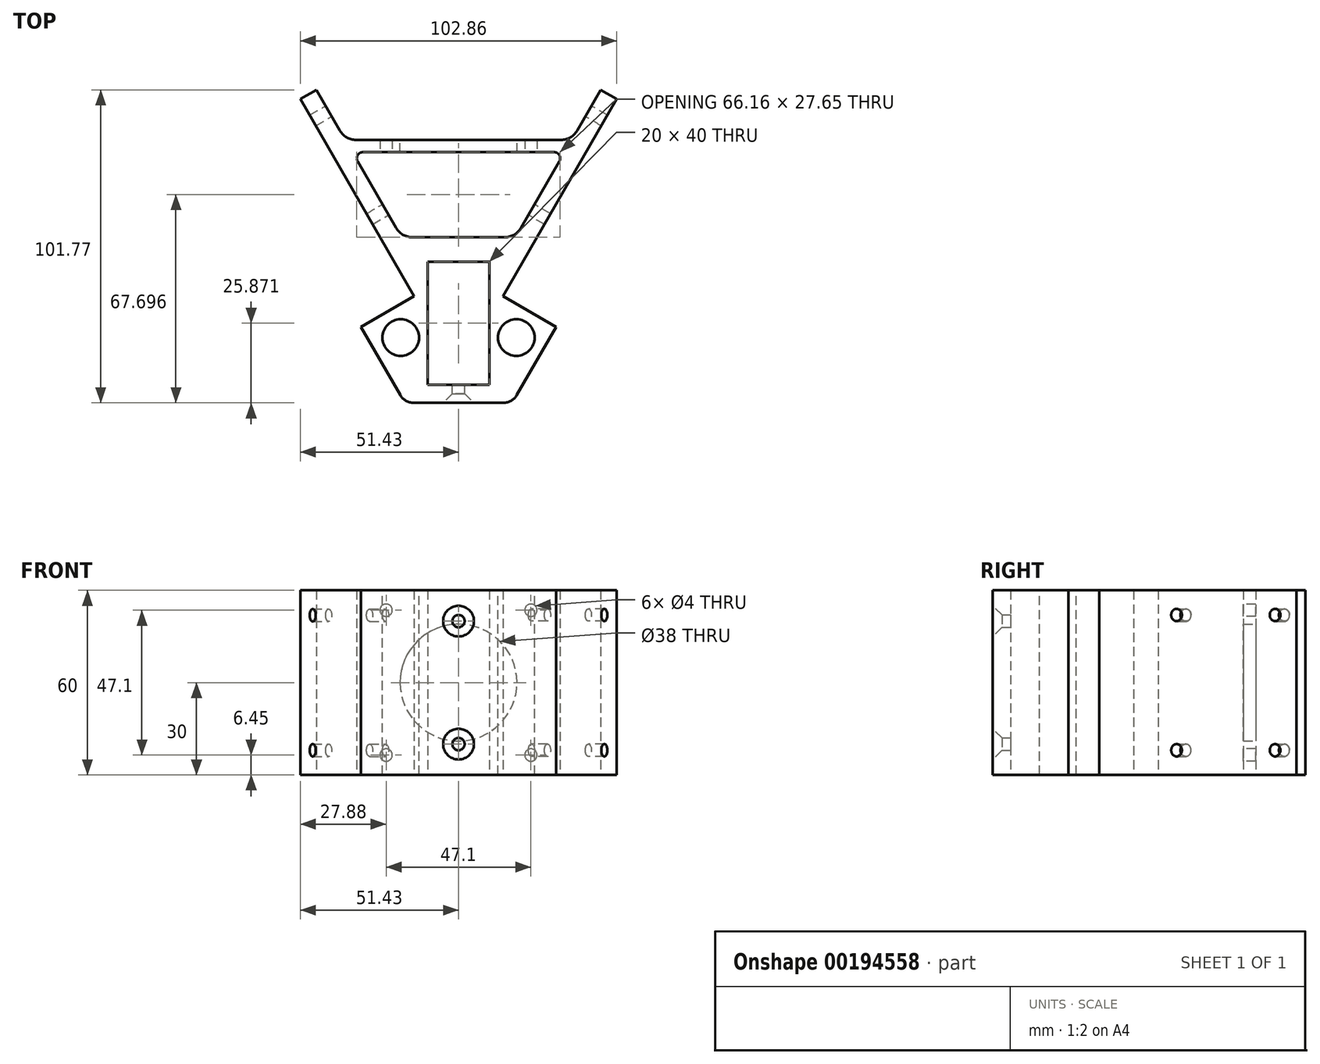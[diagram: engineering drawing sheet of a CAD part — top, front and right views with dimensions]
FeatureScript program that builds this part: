
annotation { "Feature Type Name" : "Feature", "Feature Type Description" : "" }
export const myFeature = defineFeature(function(context is Context, id is Id, definition is map)
    precondition{}
    {
        {
            var Q0;
            Q0=qCreatedBy(makeId("Top.planeOp"),FACE);
            var sketch = newSketch(context, id + "F0", { "sketchPlane" : qUnion([Q0])});
            skLineSegment(sketch, "E0", {"start": v(17.5, 30.31) * mm, "end": v(31.75, 55) * mm});
            skLineSegment(sketch, "E1", {"start": v(-17.5, 30.31) * mm, "end": v(-31.75, 55) * mm});
            skLineSegment(sketch, "E2", {"start": v(-17.5, 30.31) * mm, "end": v(17.5, 30.31) * mm});
            skLineSegment(sketch, "E3", {"start": v(-31.75, 55) * mm, "end": v(-14.43, 65) * mm});
            skLineSegment(sketch, "E4", {"start": v(-14.43, 65) * mm, "end": v(-51.43, 129.08) * mm});
            skLineSegment(sketch, "E5", {"start": v(-51.43, 129.08) * mm, "end": v(-46.23, 132.08) * mm});
            skLineSegment(sketch, "E6", {"start": v(31.75, 55) * mm, "end": v(14.43, 65) * mm});
            skLineSegment(sketch, "E7", {"start": v(14.43, 65) * mm, "end": v(51.43, 129.08) * mm});
            skLineSegment(sketch, "E8", {"start": v(51.43, 129.08) * mm, "end": v(46.23, 132.08) * mm});
            skLineSegment(sketch, "E9", {"start": v(-46.23, 132.08) * mm, "end": v(-36.85, 115.83) * mm});
            skLineSegment(sketch, "E10", {"start": v(18.58, 84.18) * mm, "end": v(34.54, 111.83) * mm});
            skLineSegment(sketch, "E11.bottom", {"start": v(-10, 36.18) * mm, "end": v(10, 36.18) * mm});
            skLineSegment(sketch, "E11.top", {"start": v(-10, 76.18) * mm, "end": v(10, 76.18) * mm});
            skLineSegment(sketch, "E11.left", {"start": v(-10, 36.18) * mm, "end": v(-10, 76.18) * mm});
            skLineSegment(sketch, "E11.right", {"start": v(10, 36.18) * mm, "end": v(10, 76.18) * mm});
            skLineSegment(sketch, "E12", {"start": v(36.85, 115.83) * mm, "end": v(-36.85, 115.83) * mm});
            skLineSegment(sketch, "E13.trimOffspring", {"start": v(36.85, 115.83) * mm, "end": v(46.23, 132.08) * mm});
            skLineSegment(sketch, "E14.trimOffspring", {"start": v(-34.54, 111.83) * mm, "end": v(-18.58, 84.18) * mm});
            skLineSegment(sketch, "E15", {"start": v(-34.54, 111.83) * mm, "end": v(34.54, 111.83) * mm});
            skLineSegment(sketch, "E16", {"start": v(18.58, 84.18) * mm, "end": v(-18.58, 84.18) * mm});
            skSolve(sketch);
        }
        {
            var Q0;
            Q0 = qSketchRegion(id + "F0", true);
            extrude(context, id + "F1", {"entities" : qUnion([Q0]), "depth" : 60 * mm});
        }
        {
            var Q0;
            Q0=makeQuery(id+"F1.opExtrude","SWEPT_EDGE",EDGE,{"disambiguationData":[OSD([sQuery(id+"F0.wireOp",EDGE,"E1"),sQuery(id+"F0.wireOp",EDGE,"E2")])]});
            var Q1;
            Q1=makeQuery(id+"F1.opExtrude","SWEPT_EDGE",EDGE,{"disambiguationData":[OSD([sQuery(id+"F0.wireOp",EDGE,"E0"),sQuery(id+"F0.wireOp",EDGE,"E2")])]});
            fillet(context, id + "F2", {"entities" : qUnion([Q0, Q1]), "radius" : 5 * mm, "tangentPropagation" : true, "allowEdgeOverflow" : false});
        }
        {
            var Q0;
            Q0=makeQuery(id+"F1.opExtrude","SWEPT_EDGE",EDGE,{"disambiguationData":[OSD([sQuery(id+"F0.wireOp",EDGE,"E10"),sQuery(id+"F0.wireOp",EDGE,"E16")])]});
            var Q1;
            Q1=makeQuery(id+"F1.opExtrude","SWEPT_EDGE",EDGE,{"disambiguationData":[OSD([sQuery(id+"F0.wireOp",EDGE,"E14.trimOffspring"),sQuery(id+"F0.wireOp",EDGE,"E16")])]});
            var Q2;
            Q2=makeQuery(id+"F1.opExtrude","SWEPT_EDGE",EDGE,{"disambiguationData":[OSD([sQuery(id+"F0.wireOp",EDGE,"E9"),sQuery(id+"F0.wireOp",EDGE,"E12")])]});
            var Q3;
            Q3=makeQuery(id+"F1.opExtrude","SWEPT_EDGE",EDGE,{"disambiguationData":[OSD([sQuery(id+"F0.wireOp",EDGE,"E12"),sQuery(id+"F0.wireOp",EDGE,"E13.trimOffspring")])]});
            fillet(context, id + "F3", {"entities" : qUnion([Q0, Q1, Q2, Q3]), "radius" : 6 * mm, "tangentPropagation" : true, "allowEdgeOverflow" : false});
        }
        {
            var Q0;
            Q0=makeQuery(id+"F1.opExtrude","SWEPT_EDGE",EDGE,{"disambiguationData":[OSD([sQuery(id+"F0.wireOp",EDGE,"E10"),sQuery(id+"F0.wireOp",EDGE,"E15")])]});
            var Q1;
            Q1=makeQuery(id+"F1.opExtrude","SWEPT_EDGE",EDGE,{"disambiguationData":[OSD([sQuery(id+"F0.wireOp",EDGE,"E14.trimOffspring"),sQuery(id+"F0.wireOp",EDGE,"E15")])]});
            fillet(context, id + "F4", {"entities" : qUnion([Q0, Q1]), "radius" : 2 * mm, "tangentPropagation" : true, "allowEdgeOverflow" : false});
        }
        {
            var Q0;
            Q0=makeQuery(id+"F1.opExtrude","CAP_FACE",FACE,{"disambiguationData":[OSD([sQuery(id+"F0.wireOp",EDGE,"E0"),sQuery(id+"F0.wireOp",EDGE,"E1"),sQuery(id+"F0.wireOp",EDGE,"E2"),sQuery(id+"F0.wireOp",EDGE,"E3"),sQuery(id+"F0.wireOp",EDGE,"E4"),sQuery(id+"F0.wireOp",EDGE,"E5"),sQuery(id+"F0.wireOp",EDGE,"E6"),sQuery(id+"F0.wireOp",EDGE,"E7"),sQuery(id+"F0.wireOp",EDGE,"E8"),sQuery(id+"F0.wireOp",EDGE,"E9"),sQuery(id+"F0.wireOp",EDGE,"E10"),sQuery(id+"F0.wireOp",EDGE,"E11.bottom"),sQuery(id+"F0.wireOp",EDGE,"E11.top"),sQuery(id+"F0.wireOp",EDGE,"E11.left"),sQuery(id+"F0.wireOp",EDGE,"E11.right"),sQuery(id+"F0.wireOp",EDGE,"E12"),sQuery(id+"F0.wireOp",EDGE,"E13.trimOffspring"),sQuery(id+"F0.wireOp",EDGE,"E14.trimOffspring"),sQuery(id+"F0.wireOp",EDGE,"E15"),sQuery(id+"F0.wireOp",EDGE,"E16")])],"isStart":false});
            var sketch = newSketch(context, id + "F5", { "sketchPlane" : qUnion([Q0])});
            skCircle(sketch, "E17", {"center": v(-18.8, 51.52) * mm, "radius": 5.97 * mm});
            skCircle(sketch, "E18", {"center": v(18.8, 51.52) * mm, "radius": 5.97 * mm});
            skSolve(sketch);
        }
        {
            var Q0;
            Q0 = qSketchRegion(id + "F5", true);
            extrude(context, id + "F6", {"entities" : qUnion([Q0]), "operationType" : NewBodyOperationType.REMOVE, "endBound" : BoundingType.THROUGH_ALL, "oppositeDirection" : true, "depth" : 25 * mm});
        }
        {
            var Q0;
            Q0=makeQuery(id+"F1.opExtrude","SWEPT_FACE",FACE,{"disambiguationData":[OSD([sQuery(id+"F0.wireOp",EDGE,"E12")])]});
            var sketch = newSketch(context, id + "F7", { "sketchPlane" : qUnion([Q0])});
            skPoint(sketch, "E19.orphan", {"position": v(0, 60) * mm});
            skPoint(sketch, "E20.trimOffspring.end.orphan", {"position": v(0, 0) * mm});
            skPoint(sketch, "E21", {"position": v(-23.55, 53.55) * mm});
            skPoint(sketch, "E22", {"position": v(23.55, 53.55) * mm});
            skPoint(sketch, "E23", {"position": v(23.55, 6.45) * mm});
            skPoint(sketch, "E24", {"position": v(-23.55, 6.45) * mm});
            skPoint(sketch, "E25", {"position": v(0, 30) * mm});
            skSolve(sketch);
        }
        {
            var Q0;
            Q0=sQuery(id+"F7.wireOp",VERTEX,"E21");
            var Q1;
            Q1=sQuery(id+"F7.wireOp",VERTEX,"E24");
            var Q2;
            Q2=sQuery(id+"F7.wireOp",VERTEX,"E23");
            var Q3;
            Q3=sQuery(id+"F7.wireOp",VERTEX,"E22");
            var Q4;
            Q4=makeQuery(id+"F1.opExtrude","SWEPT_BODY",BODY,{"disambiguationData":[OSD([sQuery(id+"F0.wireOp",EDGE,"E0"),sQuery(id+"F0.wireOp",EDGE,"E1"),sQuery(id+"F0.wireOp",EDGE,"E2"),sQuery(id+"F0.wireOp",EDGE,"E3"),sQuery(id+"F0.wireOp",EDGE,"E4"),sQuery(id+"F0.wireOp",EDGE,"E5"),sQuery(id+"F0.wireOp",EDGE,"E6"),sQuery(id+"F0.wireOp",EDGE,"E7"),sQuery(id+"F0.wireOp",EDGE,"E8"),sQuery(id+"F0.wireOp",EDGE,"E9"),sQuery(id+"F0.wireOp",EDGE,"E10"),sQuery(id+"F0.wireOp",EDGE,"E11.bottom"),sQuery(id+"F0.wireOp",EDGE,"E11.top"),sQuery(id+"F0.wireOp",EDGE,"E11.left"),sQuery(id+"F0.wireOp",EDGE,"E11.right"),sQuery(id+"F0.wireOp",EDGE,"E12"),sQuery(id+"F0.wireOp",EDGE,"E13.trimOffspring"),sQuery(id+"F0.wireOp",EDGE,"E14.trimOffspring"),sQuery(id+"F0.wireOp",EDGE,"E15"),sQuery(id+"F0.wireOp",EDGE,"E16")])]});
            hole(context, id + "F8", {"style" : HoleStyle.SIMPLE, "endStyle" : HoleEndStyle.BLIND, "holeDiameter" : 4 * mm, "holeDepth" : 12 * mm, "locations" : qUnion([Q0, Q1, Q2, Q3]), "scope" : qUnion([Q4]), "startStyle" : HoleStartStyle.PART});
        }
        {
            var Q0;
            Q0=makeQuery(id+"F1.opExtrude","SWEPT_FACE",FACE,{"disambiguationData":[OSD([sQuery(id+"F0.wireOp",EDGE,"E12")])]});
            var sketch = newSketch(context, id + "F9", { "sketchPlane" : qUnion([Q0])});
            skCircle(sketch, "E26", {"center": v(0, 30) * mm, "radius": 19 * mm});
            skPoint(sketch, "E26.centerSnap0", {"position": v(-33.39, 30) * mm});
            skSolve(sketch);
        }
        {
            var Q0;
            Q0 = qSketchRegion(id + "F9", true);
            extrude(context, id + "F10", {"entities" : qUnion([Q0]), "operationType" : NewBodyOperationType.REMOVE, "oppositeDirection" : true, "depth" : 25 * mm});
        }
        {
            var Q0;
            Q0=makeQuery(id+"F1.opExtrude","SWEPT_FACE",FACE,{"disambiguationData":[OSD([sQuery(id+"F0.wireOp",EDGE,"E7")])]});
            var sketch = newSketch(context, id + "F11", { "sketchPlane" : qUnion([Q0])});
            skPoint(sketch, "E27", {"position": v(129.5, 8) * mm});
            skPoint(sketch, "E28", {"position": v(129.5, 52) * mm});
            skPoint(sketch, "E29", {"position": v(92.5, 52) * mm});
            skPoint(sketch, "E30", {"position": v(92.5, 8) * mm});
            skSolve(sketch);
        }
        {
            var Q0;
            Q0=sQuery(id+"F11.wireOp",VERTEX,"E29");
            var Q1;
            Q1=sQuery(id+"F11.wireOp",VERTEX,"E28");
            var Q2;
            Q2=sQuery(id+"F11.wireOp",VERTEX,"E30");
            var Q3;
            Q3=sQuery(id+"F11.wireOp",VERTEX,"E27");
            var Q4;
            Q4=makeQuery(id+"F1.opExtrude","SWEPT_BODY",BODY,{"disambiguationData":[OSD([sQuery(id+"F0.wireOp",EDGE,"E0"),sQuery(id+"F0.wireOp",EDGE,"E1"),sQuery(id+"F0.wireOp",EDGE,"E2"),sQuery(id+"F0.wireOp",EDGE,"E3"),sQuery(id+"F0.wireOp",EDGE,"E4"),sQuery(id+"F0.wireOp",EDGE,"E5"),sQuery(id+"F0.wireOp",EDGE,"E6"),sQuery(id+"F0.wireOp",EDGE,"E7"),sQuery(id+"F0.wireOp",EDGE,"E8"),sQuery(id+"F0.wireOp",EDGE,"E9"),sQuery(id+"F0.wireOp",EDGE,"E10"),sQuery(id+"F0.wireOp",EDGE,"E11.bottom"),sQuery(id+"F0.wireOp",EDGE,"E11.top"),sQuery(id+"F0.wireOp",EDGE,"E11.left"),sQuery(id+"F0.wireOp",EDGE,"E11.right"),sQuery(id+"F0.wireOp",EDGE,"E12"),sQuery(id+"F0.wireOp",EDGE,"E13.trimOffspring"),sQuery(id+"F0.wireOp",EDGE,"E14.trimOffspring"),sQuery(id+"F0.wireOp",EDGE,"E15"),sQuery(id+"F0.wireOp",EDGE,"E16")])]});
            hole(context, id + "F12", {"style" : HoleStyle.SIMPLE, "endStyle" : HoleEndStyle.BLIND, "holeDiameter" : 4 * mm, "holeDepth" : 12 * mm, "locations" : qUnion([Q0, Q1, Q2, Q3]), "scope" : qUnion([Q4]), "startStyle" : HoleStartStyle.PART});
        }
        {
            var Q0;
            Q0=makeQuery(id+"F1.opExtrude","SWEPT_FACE",FACE,{"disambiguationData":[OSD([sQuery(id+"F0.wireOp",EDGE,"E4")])]});
            var sketch = newSketch(context, id + "F13", { "sketchPlane" : qUnion([Q0])});
            skPoint(sketch, "E31", {"position": v(-129.5, 8) * mm});
            skPoint(sketch, "E32", {"position": v(-129.5, 51.9) * mm});
            skPoint(sketch, "E33", {"position": v(-92.5, 51.9) * mm});
            skPoint(sketch, "E34", {"position": v(-92.5, 8) * mm});
            skSolve(sketch);
        }
        {
            var Q0;
            Q0=sQuery(id+"F13.wireOp",VERTEX,"E34");
            var Q1;
            Q1=sQuery(id+"F13.wireOp",VERTEX,"E31");
            var Q2;
            Q2=sQuery(id+"F13.wireOp",VERTEX,"E33");
            var Q3;
            Q3=sQuery(id+"F13.wireOp",VERTEX,"E32");
            var Q4;
            Q4=makeQuery(id+"F1.opExtrude","SWEPT_BODY",BODY,{"disambiguationData":[OSD([sQuery(id+"F0.wireOp",EDGE,"E0"),sQuery(id+"F0.wireOp",EDGE,"E1"),sQuery(id+"F0.wireOp",EDGE,"E2"),sQuery(id+"F0.wireOp",EDGE,"E3"),sQuery(id+"F0.wireOp",EDGE,"E4"),sQuery(id+"F0.wireOp",EDGE,"E5"),sQuery(id+"F0.wireOp",EDGE,"E6"),sQuery(id+"F0.wireOp",EDGE,"E7"),sQuery(id+"F0.wireOp",EDGE,"E8"),sQuery(id+"F0.wireOp",EDGE,"E9"),sQuery(id+"F0.wireOp",EDGE,"E10"),sQuery(id+"F0.wireOp",EDGE,"E11.bottom"),sQuery(id+"F0.wireOp",EDGE,"E11.top"),sQuery(id+"F0.wireOp",EDGE,"E11.left"),sQuery(id+"F0.wireOp",EDGE,"E11.right"),sQuery(id+"F0.wireOp",EDGE,"E12"),sQuery(id+"F0.wireOp",EDGE,"E13.trimOffspring"),sQuery(id+"F0.wireOp",EDGE,"E14.trimOffspring"),sQuery(id+"F0.wireOp",EDGE,"E15"),sQuery(id+"F0.wireOp",EDGE,"E16")])]});
            hole(context, id + "F14", {"style" : HoleStyle.SIMPLE, "endStyle" : HoleEndStyle.BLIND, "holeDiameter" : 4 * mm, "holeDepth" : 12 * mm, "locations" : qUnion([Q0, Q1, Q2, Q3]), "scope" : qUnion([Q4]), "startStyle" : HoleStartStyle.PART});
        }
        {
            var Q0;
            Q0=makeQuery(id+"F1.opExtrude","SWEPT_FACE",FACE,{"disambiguationData":[OSD([sQuery(id+"F0.wireOp",EDGE,"E2")])]});
            var sketch = newSketch(context, id + "F15", { "sketchPlane" : qUnion([Q0])});
            skPoint(sketch, "E35", {"position": v(0, 10) * mm});
            skPoint(sketch, "E36", {"position": v(0, 50) * mm});
            skSolve(sketch);
        }
        {
            var Q0;
            Q0=sQuery(id+"F15.wireOp",VERTEX,"E35");
            var Q1;
            Q1=sQuery(id+"F15.wireOp",VERTEX,"E36");
            var Q2;
            Q2=makeQuery(id+"F1.opExtrude","SWEPT_BODY",BODY,{"disambiguationData":[OSD([sQuery(id+"F0.wireOp",EDGE,"E0"),sQuery(id+"F0.wireOp",EDGE,"E1"),sQuery(id+"F0.wireOp",EDGE,"E2"),sQuery(id+"F0.wireOp",EDGE,"E3"),sQuery(id+"F0.wireOp",EDGE,"E4"),sQuery(id+"F0.wireOp",EDGE,"E5"),sQuery(id+"F0.wireOp",EDGE,"E6"),sQuery(id+"F0.wireOp",EDGE,"E7"),sQuery(id+"F0.wireOp",EDGE,"E8"),sQuery(id+"F0.wireOp",EDGE,"E9"),sQuery(id+"F0.wireOp",EDGE,"E10"),sQuery(id+"F0.wireOp",EDGE,"E11.bottom"),sQuery(id+"F0.wireOp",EDGE,"E11.top"),sQuery(id+"F0.wireOp",EDGE,"E11.left"),sQuery(id+"F0.wireOp",EDGE,"E11.right"),sQuery(id+"F0.wireOp",EDGE,"E12"),sQuery(id+"F0.wireOp",EDGE,"E13.trimOffspring"),sQuery(id+"F0.wireOp",EDGE,"E14.trimOffspring"),sQuery(id+"F0.wireOp",EDGE,"E15"),sQuery(id+"F0.wireOp",EDGE,"E16")])]});
            hole(context, id + "F16", {"style" : HoleStyle.C_SINK, "endStyle" : HoleEndStyle.BLIND, "holeDiameter" : 4 * mm, "cSinkDiameter" : 10 * mm, "cSinkAngle" : 90 * degree, "holeDepth" : 12 * mm, "locations" : qUnion([Q0, Q1]), "scope" : qUnion([Q2]), "startStyle" : HoleStartStyle.PART});
        }
    });
